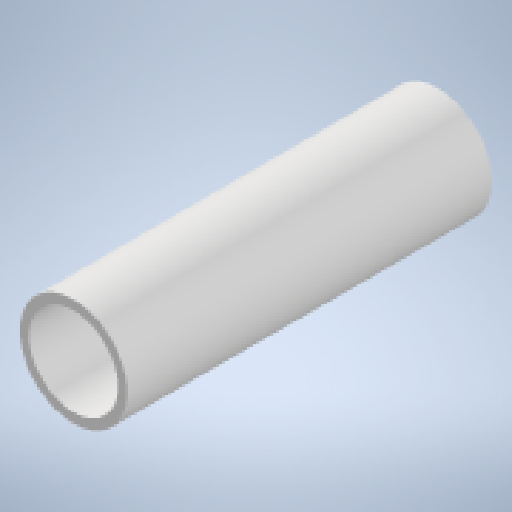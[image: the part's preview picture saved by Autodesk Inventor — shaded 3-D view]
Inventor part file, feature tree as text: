
AUTODESK INVENTOR PART (.ipt)
format: ipt  version: 2023.1 (Build 271208000, 208)  size: 141,824 bytes
history: native  units: mm
features: revolve x1, sketch x1
ambient origin geometry x8: Origin, YZ Plane, XZ Plane, XY Plane, X Axis, Y Axis, Z Axis, Center Point
bodies: Solid1 (feature_tree)
feature tree (2):
  revolve  "Revolution1"  [1 undecoded]
  sketch  "Sketch1"  dims[d0=80.0mm d1=17.7mm d2=21.5mm d3=73.0mm d4=90.0deg]
note: 1 required parameter value undecoded (feature->parameter linkage not recoverable at this tier; creation-order binding heuristic only, values carry confidence <= 0.55)
